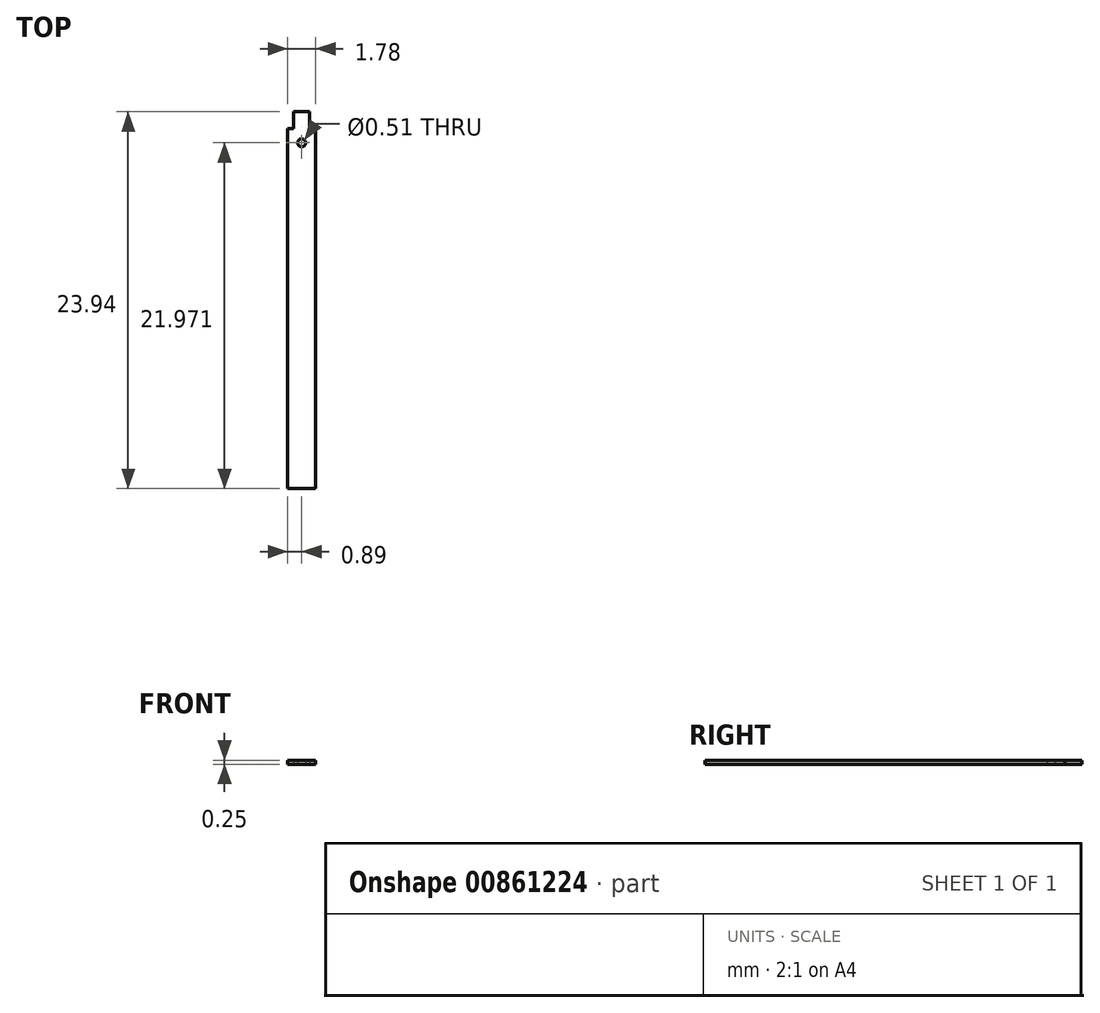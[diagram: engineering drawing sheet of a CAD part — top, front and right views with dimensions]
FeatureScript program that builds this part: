
annotation { "Feature Type Name" : "Feature", "Feature Type Description" : "" }
export const myFeature = defineFeature(function(context is Context, id is Id, definition is map)
    precondition{}
    {
        {
            var Q0;
            Q0=qCreatedBy(makeId("Top.planeOp"),FACE);
            var sketch = newSketch(context, id + "F0", { "sketchPlane" : qUnion([Q0])});
            skLineSegment(sketch, "E0.bottom", {"start": v(0.89, -11.43) * mm, "end": v(-0.89, -11.43) * mm});
            skLineSegment(sketch, "E0.top", {"start": v(0.89, 11.43) * mm, "end": v(0.5, 11.43) * mm});
            skLineSegment(sketch, "E0.left", {"start": v(0.89, -11.43) * mm, "end": v(0.89, 11.43) * mm});
            skLineSegment(sketch, "E0.right", {"start": v(-0.89, -11.43) * mm, "end": v(-0.89, 11.43) * mm});
            skPoint(sketch, "E0.middle", {"position": v(0, 0) * mm});
            skLineSegment(sketch, "E1", {"start": v(-0.5, 11.43) * mm, "end": v(-0.5, 12.5) * mm});
            skLineSegment(sketch, "E2", {"start": v(-0.5, 12.5) * mm, "end": v(0.5, 12.5) * mm});
            skLineSegment(sketch, "E3", {"start": v(0.5, 12.5) * mm, "end": v(0.5, 11.43) * mm});
            skLineSegment(sketch, "E4.trimOffspring", {"start": v(-0.5, 11.43) * mm, "end": v(-0.89, 11.43) * mm});
            skCircle(sketch, "E5", {"center": v(0, 10.54) * mm, "radius": 0.25 * mm});
            skSolve(sketch);
        }
        {
            var Q0;
            Q0 = qSketchRegion(id + "F0", true);
            extrude(context, id + "F1", {"entities" : qUnion([Q0]), "depth" : 0.25 * mm, "offsetDistance" : 25.4 * mm});
        }
    });
